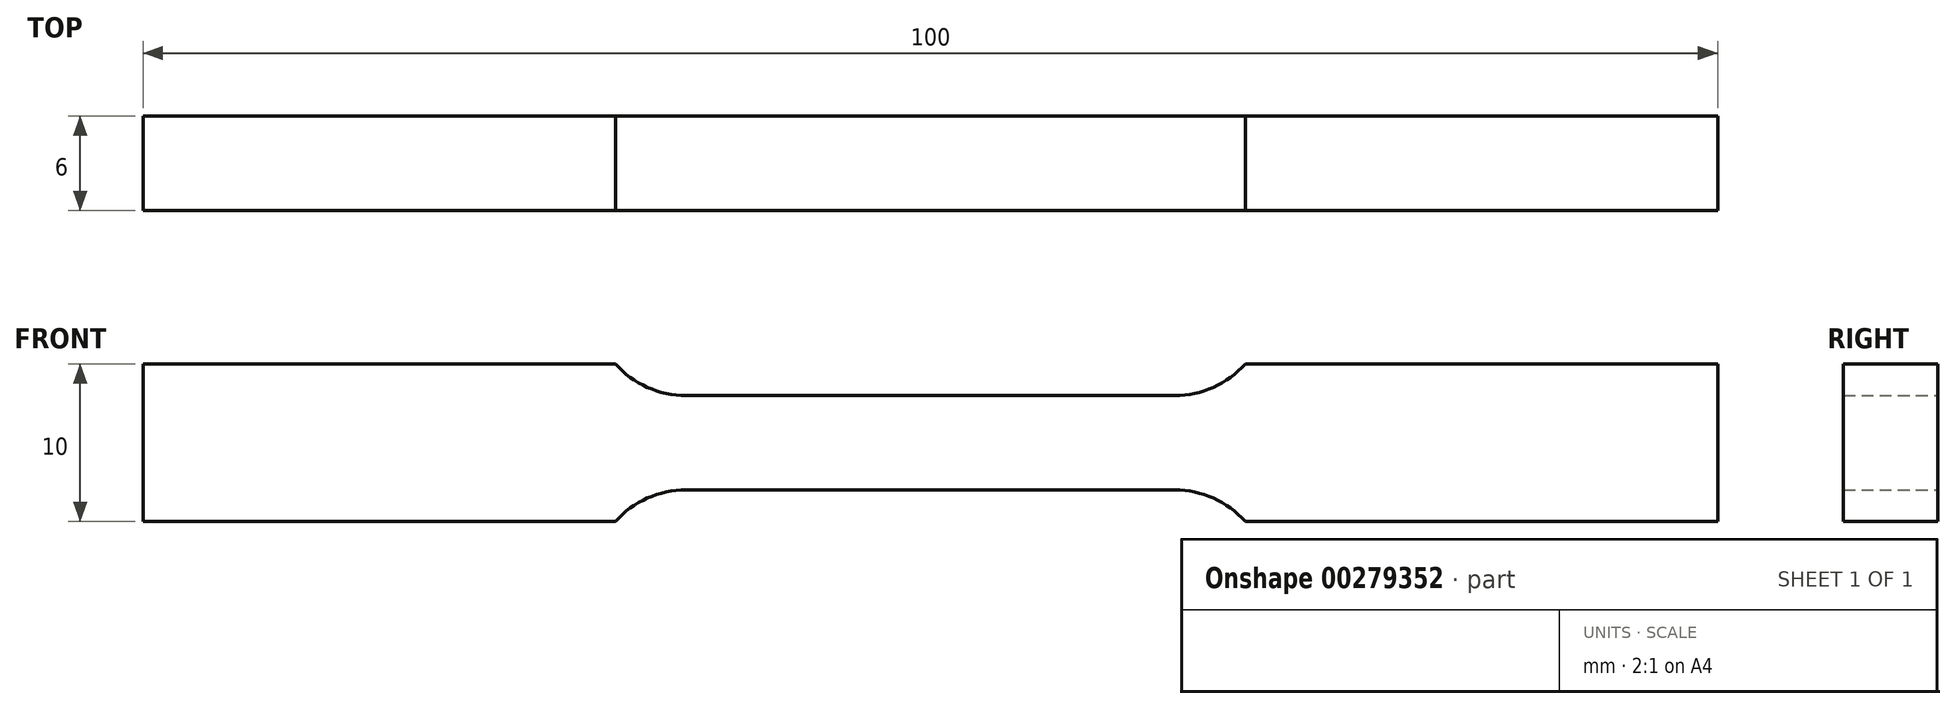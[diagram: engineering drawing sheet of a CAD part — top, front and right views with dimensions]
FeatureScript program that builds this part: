
annotation { "Feature Type Name" : "Feature", "Feature Type Description" : "" }
export const myFeature = defineFeature(function(context is Context, id is Id, definition is map)
    precondition{}
    {
        {
            var Q0;
            Q0=qCreatedBy(makeId("Front.planeOp"),FACE);
            var sketch = newSketch(context, id + "F0", { "sketchPlane" : qUnion([Q0])});
            skLineSegment(sketch, "E0", {"start": v(0, 3) * mm, "end": v(15.53, 3) * mm});
            skArc(sketch, "E1", {"start": v(15.53, 3) * mm, "mid": v(17.98, 3.52) * mm, "end": v(20, 5) * mm});
            skLineSegment(sketch, "E2", {"start": v(20, 5) * mm, "end": v(50, 5) * mm});
            skLineSegment(sketch, "E3", {"start": v(50, 5) * mm, "end": v(50, 0) * mm});
            skLineSegment(sketch, "E4.MirrorCS", {"start": v(0, -3) * mm, "end": v(15.53, -3) * mm});
            skLineSegment(sketch, "E5.MirrorCS", {"start": v(50, -5) * mm, "end": v(50, 0) * mm});
            skLineSegment(sketch, "E6.MirrorCS", {"start": v(20, -5) * mm, "end": v(50, -5) * mm});
            skArc(sketch, "E7.MirrorCS", {"start": v(15.53, -3) * mm, "mid": v(17.98, -3.52) * mm, "end": v(20, -5) * mm});
            skArc(sketch, "E8.MirrorCS", {"start": v(-15.53, -3) * mm, "mid": v(-17.98, -3.52) * mm, "end": v(-20, -5) * mm});
            skLineSegment(sketch, "E9.MirrorCS", {"start": v(-20, -5) * mm, "end": v(-50, -5) * mm});
            skArc(sketch, "E10.MirrorCS", {"start": v(-15.53, 3) * mm, "mid": v(-17.98, 3.52) * mm, "end": v(-20, 5) * mm});
            skLineSegment(sketch, "E11.MirrorCS", {"start": v(-20, 5) * mm, "end": v(-50, 5) * mm});
            skLineSegment(sketch, "E12.MirrorCS", {"start": v(-50, -5) * mm, "end": v(-50, 0) * mm});
            skLineSegment(sketch, "E13.MirrorCS", {"start": v(0, -3) * mm, "end": v(-15.53, -3) * mm});
            skLineSegment(sketch, "E14.MirrorCS", {"start": v(-50, 5) * mm, "end": v(-50, 0) * mm});
            skLineSegment(sketch, "E15.MirrorCS", {"start": v(0, 3) * mm, "end": v(-15.53, 3) * mm});
            skSolve(sketch);
        }
        {
            var Q0;
            Q0=makeQuery(id+"F0.imprint","IMPRINT",FACE,{"disambiguationData":[TD([[makeQuery(id+"F0.imprint","IMPRINT",EDGE,{"derivedFrom":sQuery(id+"F0.wireOp",EDGE,"E0")}),-1.0]])]});
            extrude(context, id + "F1", {"entities" : qUnion([Q0]), "depth" : 6 * mm});
        }
    });
